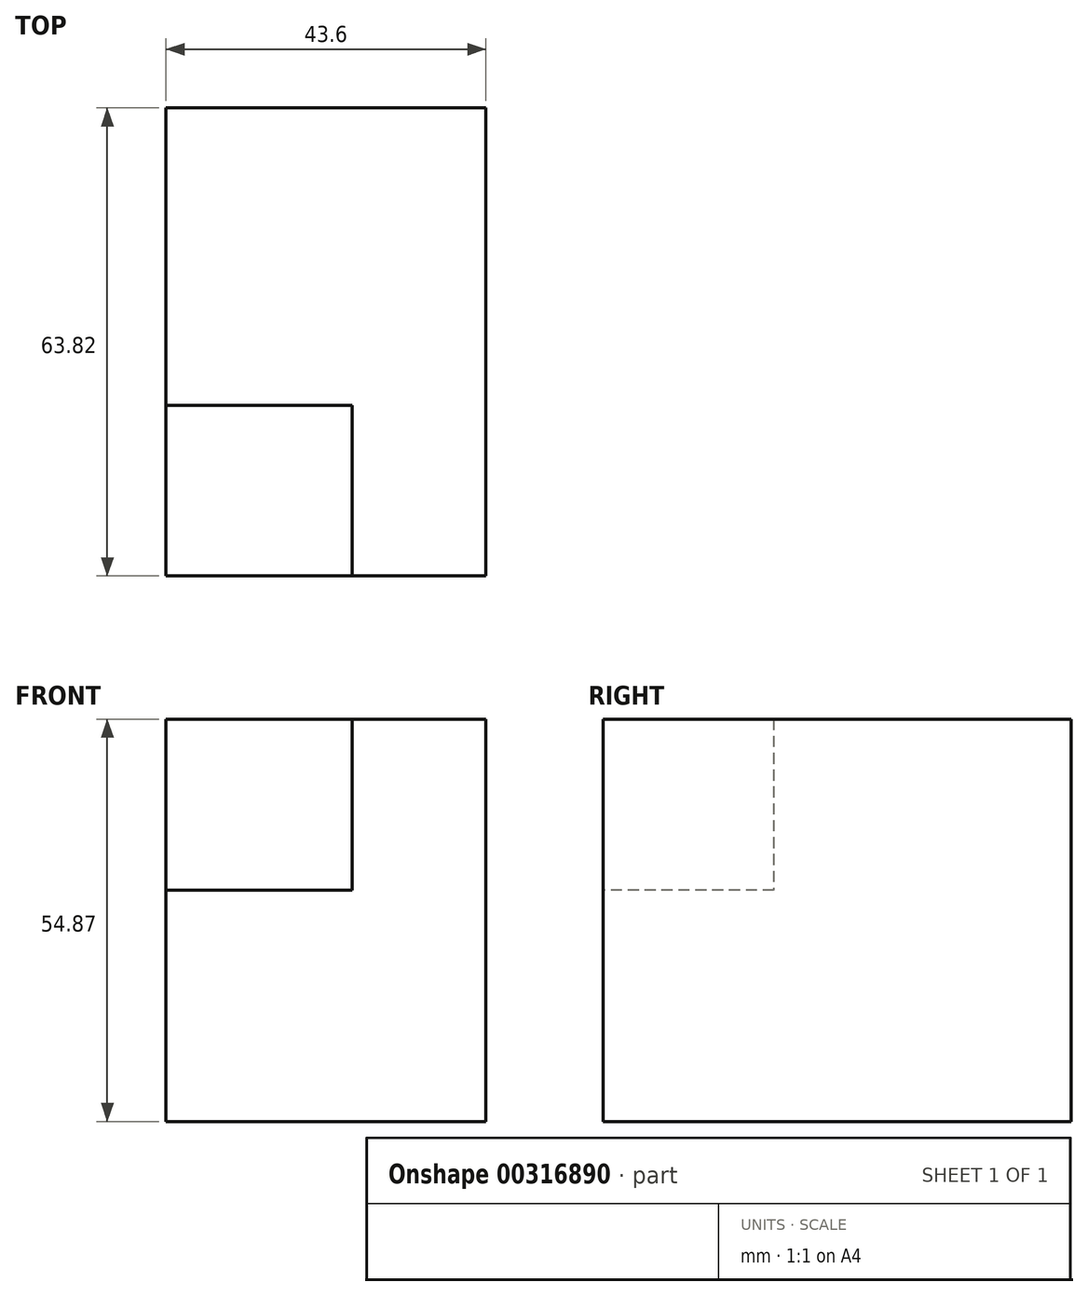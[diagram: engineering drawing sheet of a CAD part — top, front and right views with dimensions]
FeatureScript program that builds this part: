
annotation { "Feature Type Name" : "Feature", "Feature Type Description" : "" }
export const myFeature = defineFeature(function(context is Context, id is Id, definition is map)
    precondition{}
    {
        {
            var Q0;
            Q0=qCreatedBy(makeId("Front.planeOp"),FACE);
            var sketch = newSketch(context, id + "F0", { "sketchPlane" : qUnion([Q0])});
            skLineSegment(sketch, "E0.bottom", {"start": v(0, 54.87) * mm, "end": v(43.6, 54.87) * mm});
            skLineSegment(sketch, "E0.top", {"start": v(0, 0) * mm, "end": v(43.6, 0) * mm});
            skLineSegment(sketch, "E0.left", {"start": v(0, 54.87) * mm, "end": v(0, 0) * mm});
            skLineSegment(sketch, "E0.right", {"start": v(43.6, 54.87) * mm, "end": v(43.6, 0) * mm});
            skSolve(sketch);
        }
        {
            var Q0;
            Q0=makeQuery(id+"F0.imprint","IMPRINT",FACE,{"disambiguationData":[TD([[makeQuery(id+"F0.imprint","IMPRINT",EDGE,{"derivedFrom":sQuery(id+"F0.wireOp",EDGE,"E0.bottom")}),-1.0]])]});
            var Q1;
            Q1=sQuery(id+"F0.wireOp",EDGE,"E0.bottom");
            var Q2;
            Q2=sQuery(id+"F0.wireOp",EDGE,"E0.right");
            var Q3;
            Q3=sQuery(id+"F0.wireOp",EDGE,"E0.top");
            extrude(context, id + "F1", {"entities" : qUnion([Q0]), "surfaceEntities" : qUnion([Q1, Q2, Q3]), "depth" : 63.82 * mm});
        }
        {
            var Q0;
            Q0=makeQuery(id+"F1.opExtrude","SWEPT_FACE",FACE,{"disambiguationData":[OSD([sQuery(id+"F0.wireOp",EDGE,"E0.left")])]});
            var sketch = newSketch(context, id + "F2", { "sketchPlane" : qUnion([Q0])});
            skLineSegment(sketch, "E1.bottom", {"start": v(40.56, 31.51) * mm, "end": v(63.82, 31.51) * mm});
            skLineSegment(sketch, "E1.top", {"start": v(40.56, 54.87) * mm, "end": v(63.82, 54.87) * mm});
            skLineSegment(sketch, "E1.left", {"start": v(40.56, 54.87) * mm, "end": v(40.56, 31.51) * mm});
            skLineSegment(sketch, "E1.right", {"start": v(63.82, 54.87) * mm, "end": v(63.82, 31.51) * mm});
            skSolve(sketch);
        }
        {
            var Q0;
            Q0=makeQuery(id+"F2.imprint","IMPRINT",FACE,{"disambiguationData":[TD([[makeQuery(id+"F2.imprint","IMPRINT",EDGE,{"derivedFrom":sQuery(id+"F2.wireOp",EDGE,"E1.bottom")}),1.0]])]});
            extrude(context, id + "F3", {"entities" : qUnion([Q0]), "operationType" : NewBodyOperationType.REMOVE, "oppositeDirection" : true, "depth" : 25.4 * mm});
        }
    });
